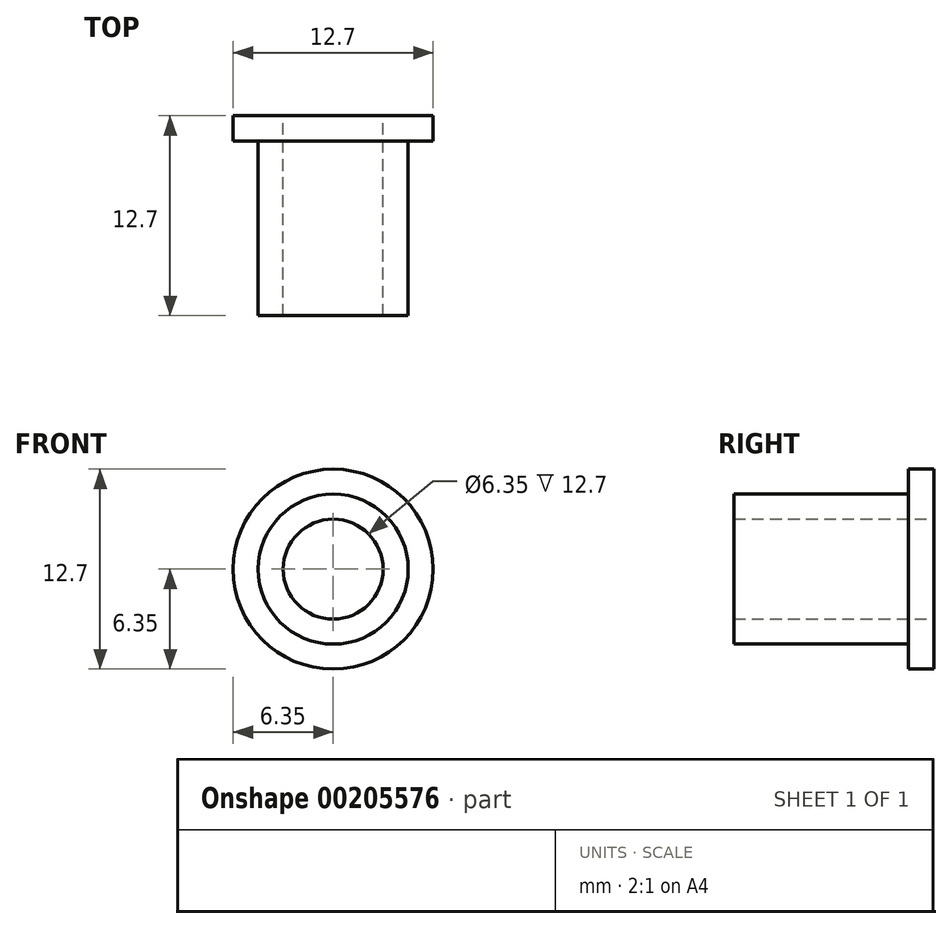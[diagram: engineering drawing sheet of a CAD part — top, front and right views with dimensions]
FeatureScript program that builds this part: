
annotation { "Feature Type Name" : "Feature", "Feature Type Description" : "" }
export const myFeature = defineFeature(function(context is Context, id is Id, definition is map)
    precondition{}
    {
        {
            var Q0;
            Q0=qCreatedBy(makeId("Front.planeOp"),FACE);
            var sketch = newSketch(context, id + "F0", { "sketchPlane" : qUnion([Q0])});
            skCircle(sketch, "E0", {"center": v(0, 0) * mm, "radius": 6.35 * mm});
            skSolve(sketch);
        }
        {
            var Q0;
            Q0=qSketchRegion(id+"F0",true);
            extrude(context, id + "F1", {"entities" : qUnion([Q0]), "oppositeDirection" : true, "depth" : 1.6 * mm});
        }
        {
            var Q0;
            Q0=makeQuery(id+"F1.opExtrude","CAP_FACE",FACE,{"disambiguationData":[OSD([sQuery(id+"F0.wireOp",EDGE,"E0")])],"isStart":true});
            var sketch = newSketch(context, id + "F2", { "sketchPlane" : qUnion([Q0])});
            skCircle(sketch, "E1", {"center": v(0, 0) * mm, "radius": 4.76 * mm});
            skSolve(sketch);
        }
        {
            var Q0;
            Q0=qSketchRegion(id+"F2",true);
            extrude(context, id + "F3", {"entities" : qUnion([Q0]), "operationType" : NewBodyOperationType.ADD, "depth" : 11.1 * mm});
        }
        {
            var Q0;
            Q0=makeQuery(id+"F1.opExtrude","CAP_FACE",FACE,{"disambiguationData":[OSD([sQuery(id+"F0.wireOp",EDGE,"E0")])],"isStart":true});
            var sketch = newSketch(context, id + "F4", { "sketchPlane" : qUnion([Q0])});
            skCircle(sketch, "E2", {"center": v(0, 0) * mm, "radius": 3.18 * mm});
            skSolve(sketch);
        }
        {
            var Q0;
            Q0=qSketchRegion(id+"F4",true);
            extrude(context, id + "F5", {"entities" : qUnion([Q0]), "operationType" : NewBodyOperationType.REMOVE, "depth" : 38.1 * mm, "symmetric" : true});
        }
    });
